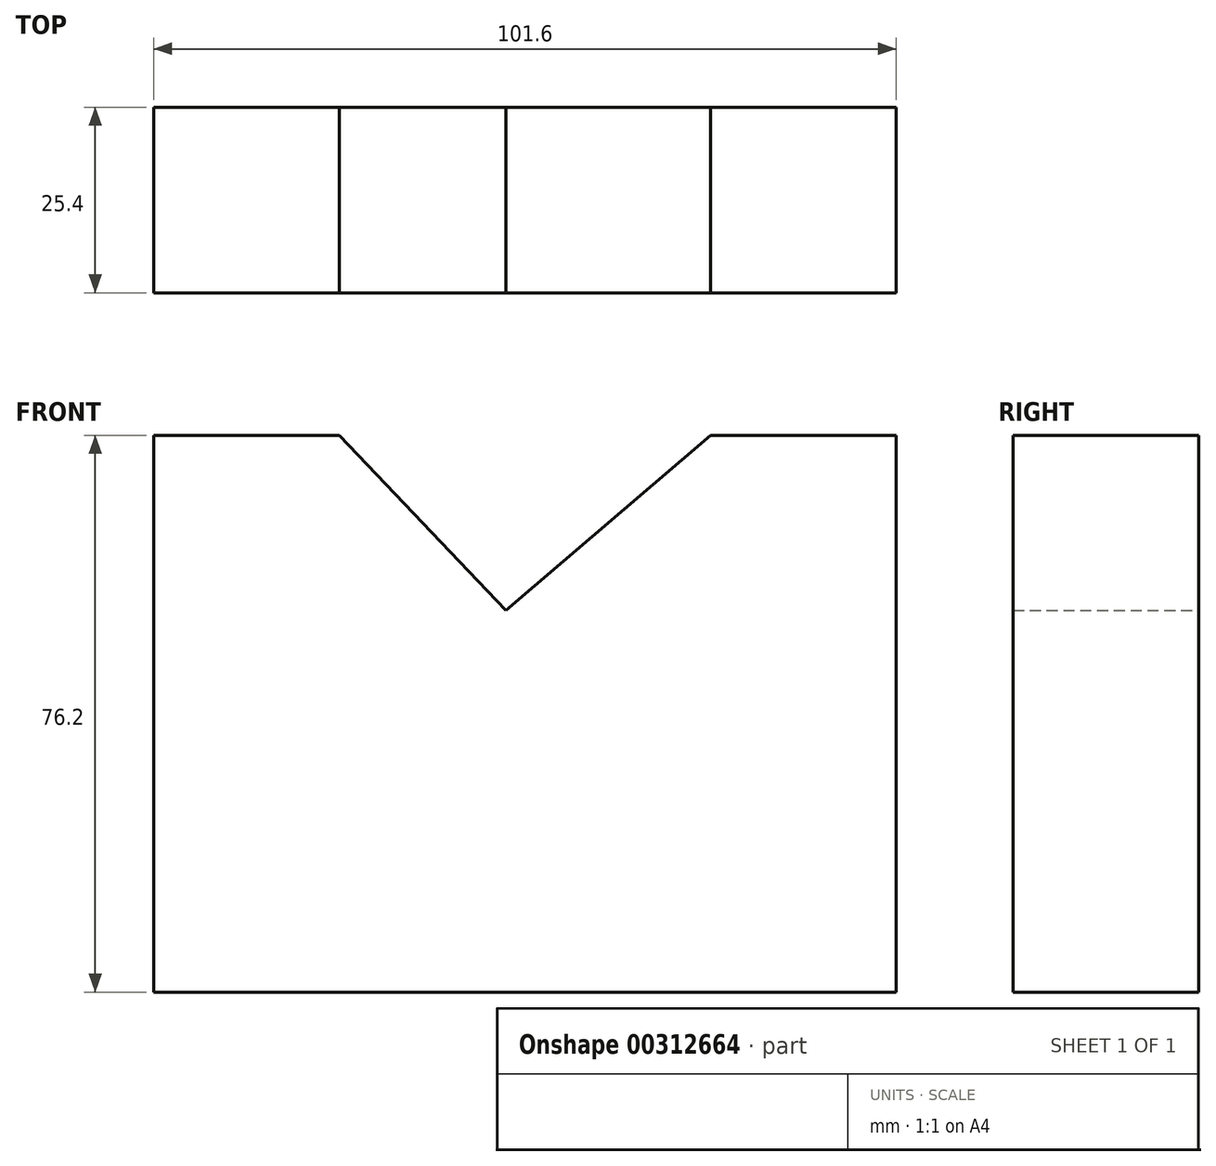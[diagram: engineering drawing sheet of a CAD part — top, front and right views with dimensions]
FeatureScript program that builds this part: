
annotation { "Feature Type Name" : "Feature", "Feature Type Description" : "" }
export const myFeature = defineFeature(function(context is Context, id is Id, definition is map)
    precondition{}
    {
        {
            var Q0;
            Q0=qCreatedBy(makeId("Front.planeOp"),FACE);
            var sketch = newSketch(context, id + "F0", { "sketchPlane" : qUnion([Q0])});
            skLineSegment(sketch, "E0", {"start": v(28.03, 38.81) * mm, "end": v(53.43, 38.81) * mm});
            skLineSegment(sketch, "E1", {"start": v(53.43, 38.81) * mm, "end": v(53.43, -37.39) * mm});
            skLineSegment(sketch, "E2", {"start": v(53.43, -37.39) * mm, "end": v(-48.17, -37.39) * mm});
            skLineSegment(sketch, "E3", {"start": v(-48.17, -37.39) * mm, "end": v(-48.17, 38.81) * mm});
            skLineSegment(sketch, "E4", {"start": v(-48.17, 38.81) * mm, "end": v(-22.77, 38.81) * mm});
            skLineSegment(sketch, "E5", {"start": v(-22.77, 38.81) * mm, "end": v(0, 14.87) * mm});
            skLineSegment(sketch, "E6", {"start": v(0, 14.87) * mm, "end": v(28.03, 38.81) * mm});
            skSolve(sketch);
        }
        {
            var Q0;
            Q0 = qSketchRegion(id + "F0", true);
            extrude(context, id + "F1", {"entities" : qUnion([Q0]), "depth" : 25.4 * mm});
        }
    });
